# Revit family: FP-Revit20-en-OM30S_OS30S_CompactCombiSpeedOven-CompactCombiSteamOven-0-90005522A-US-CA
name_source: partatom
category: Specialty Equipment
units: mm (PartAtom-declared; Revit-internal decimal feet)

## family parameters
Always vertical = Yes
Cut with Voids When Loaded = Yes
OmniClass Number = 23.40.40.14.17.11
OmniClass Title = Cookers, Ovens, Stoves
Part Type = Normal
Room Calculation Point = No
Round Connector Dimension = Use Diameter
Shared = No
Work Plane-Based = No

## types (15) — shared parameters
Cavity - Depth = 550 mm
Cavity - Height = 440 mm  [stored 1.44357 ft]
Cavity - Width = 724 mm  [stored 2.37533 ft]
Chassis - Depth = 545 mm  [stored 1.78806 ft]
Chassis - Height = 435 mm  [stored 1.42717 ft]
Chassis - Width = 555 mm  [stored 1.82087 ft]
Connector Description - Electrical = 208 or 240 V, 60 Hz, 15 A circuit
Manufacturer = Fisher & Paykel Appliances
Material - Body = Fisher & Paykel - Grey
Material - Clearance Required = Fisher & Paykel - Clearance Required
Opening - Height = 460 mm  [stored 1.50919 ft]
Opening - Width = 762 mm  [stored 2.5 ft]
Product - Height = 458 mm
Product - Width = 758 mm  [stored 2.48688 ft]
URL = www.fisherpaykel.com
zero-valued in all types: Default Elevation

## per-type parameters (varying)
| type | Control Panel - Depth | Description | Display - Height | Display - Offset | Display - Width | Model | Opening - Depth | Power Supply - Offset | Product - Depth | Style | Type Comments | Visibility - Microwave | Visibility - Steam |
| OM30NPUX3 | 24 mm  [stored 0.0787402 ft] | 30" Convection Speed Oven | 54 mm  [stored 0.177165 ft] | 23 mm  [stored 0.0754593 ft] | 154 mm  [stored 0.505249 ft] | OM30NPUX3 | 24 mm  [stored 0.0787402 ft] | 498 mm | 569 mm | 30in-76cm Fronts : 30in Front Professional | Compact, Professional, Stainless | Yes | No |
| OM30NCUDX3 | 20 mm  [stored 0.0656168 ft] | 30" Convection Speed Oven | 54 mm  [stored 0.177165 ft] | 23 mm  [stored 0.0754593 ft] | 154 mm  [stored 0.505249 ft] | OM30NCUDX3 | 20 mm  [stored 0.0656168 ft] | 175 mm | 565 mm | 30in-76cm Fronts : 30in Front Contemporary w Dial (Stainless) | Compact, Contemporary, Stainless | Yes | No |
| OM30NMUG3 | 20 mm  [stored 0.0656168 ft] | 30" Convection Speed Oven | 54 mm  [stored 0.177165 ft] | 23 mm  [stored 0.0754593 ft] | 154 mm  [stored 0.505249 ft] | OM30NMUG3
OM30NMUB3 | 20 mm  [stored 0.0656168 ft] | 175 mm | 565 mm | 30in-76cm Fronts : 30in Front Minimal (Grey) | Compact, Minimal, Grey | Yes | No |
| OM30NMUNB3 | 20 mm  [stored 0.0656168 ft] | 30" Convection Speed Oven | 54 mm  [stored 0.177165 ft] | 23 mm  [stored 0.0754593 ft] | 154 mm  [stored 0.505249 ft] | OM30NMUNB3 | 20 mm  [stored 0.0656168 ft] | 175 mm | 565 mm | 30in-76cm Fronts : 30in Front Minimal (Black) No Handle | Compact, Minimal, Black, Handleless | Yes | No |
| OM30NMUNG3 | 20 mm  [stored 0.0656168 ft] | 30" Convection Speed Oven | 54 mm  [stored 0.177165 ft] | 23 mm  [stored 0.0754593 ft] | 154 mm  [stored 0.505249 ft] | OM30NMUNG3 | 20 mm  [stored 0.0656168 ft] | 175 mm | 565 mm | 30in-76cm Fronts : 30in Front Minimal (Grey) No Handle | Compact, Minimal, Grey, Handleless | Yes | No |
| OM30NMUB3 | 20 mm  [stored 0.0656168 ft] | 30" Convection Speed Oven | 54 mm  [stored 0.177165 ft] | 23 mm  [stored 0.0754593 ft] | 154 mm  [stored 0.505249 ft] | OM30NMUB3 | 20 mm  [stored 0.0656168 ft] | 175 mm | 565 mm | 30in-76cm Fronts : 30in Front Minimal (Black) | Compact, Minimal, Black | Yes | No |
| OS30NPUX3 | 24 mm  [stored 0.0787402 ft] | 30" Combination Steam Oven | 54 mm  [stored 0.177165 ft] | 23 mm  [stored 0.0754593 ft] | 154 mm  [stored 0.505249 ft] | OS30NPUX3 | 24 mm  [stored 0.0787402 ft] | 498 mm | 569 mm | 30in-76cm Fronts : 30in Front Professional | Compact, Professional, Stainless | No | Yes |
| OS30NMUB3 | 20 mm  [stored 0.0656168 ft] | 30" Combination Steam Oven | 54 mm  [stored 0.177165 ft] | 23 mm  [stored 0.0754593 ft] | 154 mm  [stored 0.505249 ft] | OS30NMUB3 | 20 mm  [stored 0.0656168 ft] | 498 mm | 565 mm | 30in-76cm Fronts : 30in Front Minimal (Black) | Compact, Minimal, Black | No | Yes |
| OS30NMUG3 | 20 mm  [stored 0.0656168 ft] | 30" Combination Steam Oven | 54 mm  [stored 0.177165 ft] | 23 mm  [stored 0.0754593 ft] | 154 mm  [stored 0.505249 ft] | OS30NMUG3 | 20 mm  [stored 0.0656168 ft] | 498 mm | 565 mm | 30in-76cm Fronts : 30in Front Minimal (Grey) | Compact, Minimal, Grey | No | Yes |
| OS30NMUNB3 | 20 mm  [stored 0.0656168 ft] | 30" Combination Steam Oven | 54 mm  [stored 0.177165 ft] | 23 mm  [stored 0.0754593 ft] | 154 mm  [stored 0.505249 ft] | OS30NMUNB3 | 20 mm  [stored 0.0656168 ft] | 498 mm | 565 mm | 30in-76cm Fronts : 30in Front Minimal (Black) No Handle | Compact, Minimal, Black, Handleless | No | Yes |
| OS30NMUNG3 | 20 mm  [stored 0.0656168 ft] | 30" Combination Steam Oven | 54 mm  [stored 0.177165 ft] | 23 mm  [stored 0.0754593 ft] | 154 mm  [stored 0.505249 ft] | OS30NMUNG3 | 20 mm  [stored 0.0656168 ft] | 498 mm | 565 mm | 30in-76cm Fronts : 30in Front Minimal (Grey) No Handle | Compact, Minimal, Grey, Handleless | No | Yes |
| OS30NCUDX3 | 20 mm  [stored 0.0656168 ft] | 30" Combination Steam Oven | 54 mm  [stored 0.177165 ft] | 23 mm  [stored 0.0754593 ft] | 154 mm  [stored 0.505249 ft] | OS30NCUDX3 | 20 mm  [stored 0.0656168 ft] | 498 mm | 565 mm | 30in-76cm Fronts : 30in Front Contemporary w Dial (Stainless) | Compact, Contemporary, Stainless | No | Yes |
| OM30NCTDX3 | 20 mm  [stored 0.0656168 ft] | 30" Convection Speed Oven | 62 mm | 19 mm | 110 mm  [stored 0.360892 ft] | OM30NCTDX3 | 20 mm  [stored 0.0656168 ft] | 175 mm | 565 mm | 30in-76cm Fronts : 30in Front Contemporary w Dial (Stainless) | Compact, Contemporary, Stainless, S7 | Yes | No |
| OM30NCTDB3 | 20 mm  [stored 0.0656168 ft] | 30" Convection Speed Oven | 62 mm | 19 mm | 110 mm  [stored 0.360892 ft] | OM30NCTDB3 | 20 mm  [stored 0.0656168 ft] | 175 mm | 565 mm | 30in-76cm Fronts : 30in Front Contemporary w Dial (Black) | Compact, Contemporary, Stainless, S7 | Yes | No |
| OM30NPTX3 | 24 mm  [stored 0.0787402 ft] | 30" Convection Speed Oven | 54 mm  [stored 0.177165 ft] | 23 mm  [stored 0.0754593 ft] | 154 mm  [stored 0.505249 ft] | OM30NPTX3
OM30NPTX3 | 24 mm  [stored 0.0787402 ft] | 175 mm | 569 mm | 30in-76cm Fronts : 30in Front Professional | Compact, Professional, Stainless, S7 | Yes | No |

note: [stored X ft] marks values corroborated as IEEE doubles in the binary element streams (Revit-internal decimal feet)

## geometry (parser evidence)
native form markers: Sweep x17
no freeform markers — native parametric forms only
